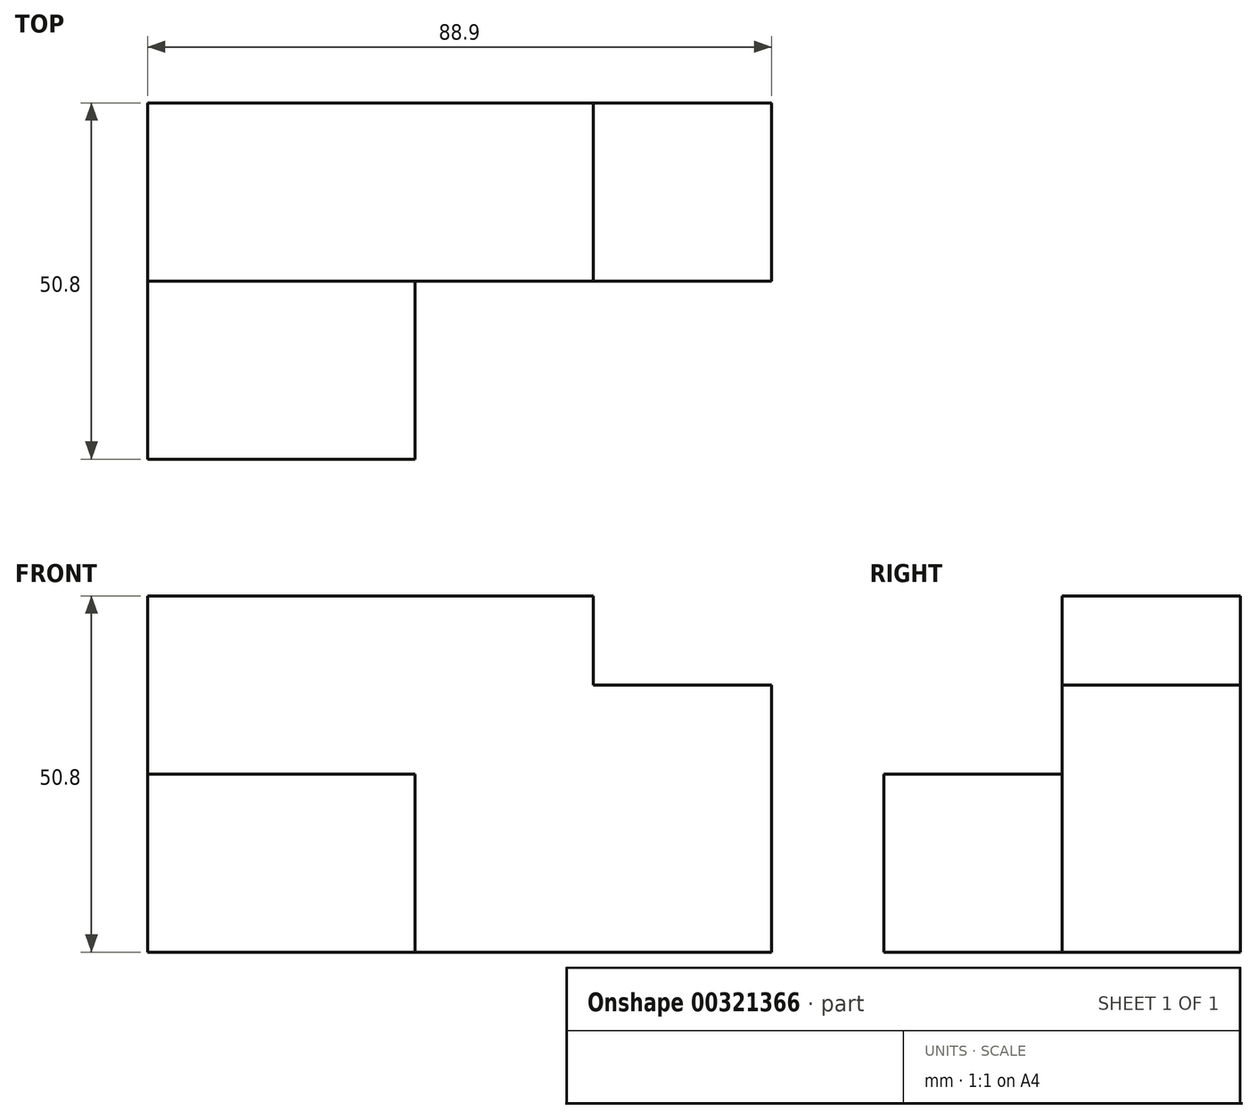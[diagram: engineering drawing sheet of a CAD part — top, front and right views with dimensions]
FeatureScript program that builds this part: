
annotation { "Feature Type Name" : "Feature", "Feature Type Description" : "" }
export const myFeature = defineFeature(function(context is Context, id is Id, definition is map)
    precondition{}
    {
        {
            var Q0;
            Q0=qCreatedBy(makeId("Front.planeOp"),FACE);
            var sketch = newSketch(context, id + "F0", { "sketchPlane" : qUnion([Q0])});
            skLineSegment(sketch, "E0", {"start": v(-32.5, 6.18) * mm, "end": v(31, 6.18) * mm});
            skLineSegment(sketch, "E1", {"start": v(31, 6.18) * mm, "end": v(31, -6.52) * mm});
            skLineSegment(sketch, "E2", {"start": v(31, -6.52) * mm, "end": v(56.4, -6.52) * mm});
            skLineSegment(sketch, "E3", {"start": v(56.4, -6.52) * mm, "end": v(56.4, -44.62) * mm});
            skLineSegment(sketch, "E4", {"start": v(56.4, -44.62) * mm, "end": v(-32.5, -44.62) * mm});
            skLineSegment(sketch, "E5", {"start": v(-32.5, -44.62) * mm, "end": v(-32.5, 6.18) * mm});
            skSolve(sketch);
        }
        {
            var Q0;
            Q0=makeQuery(id+"F0.imprint","IMPRINT",FACE,{"disambiguationData":[TD([[makeQuery(id+"F0.imprint","IMPRINT",EDGE,{"derivedFrom":sQuery(id+"F0.wireOp",EDGE,"E0")}),-1.0]])]});
            extrude(context, id + "F1", {"entities" : qUnion([Q0]), "oppositeDirection" : true, "depth" : 25.4 * mm});
        }
        {
            var Q0;
            Q0=makeQuery(id+"F1.opExtrude","CAP_FACE",FACE,{"disambiguationData":[OSD([sQuery(id+"F0.wireOp",EDGE,"E0"),sQuery(id+"F0.wireOp",EDGE,"E1"),sQuery(id+"F0.wireOp",EDGE,"E2"),sQuery(id+"F0.wireOp",EDGE,"E3"),sQuery(id+"F0.wireOp",EDGE,"E4"),sQuery(id+"F0.wireOp",EDGE,"E5")])],"isStart":true});
            var sketch = newSketch(context, id + "F2", { "sketchPlane" : qUnion([Q0])});
            skLineSegment(sketch, "E6", {"start": v(-32.5, -44.62) * mm, "end": v(-32.5, -19.22) * mm});
            skLineSegment(sketch, "E7", {"start": v(-32.5, -19.22) * mm, "end": v(5.6, -19.22) * mm});
            skLineSegment(sketch, "E8", {"start": v(5.6, -19.22) * mm, "end": v(5.6, -44.62) * mm});
            skLineSegment(sketch, "E9", {"start": v(5.6, -44.62) * mm, "end": v(-32.5, -44.62) * mm});
            skSolve(sketch);
        }
        {
            var Q0;
            Q0=makeQuery(id+"F2.imprint","IMPRINT",FACE,{"disambiguationData":[TD([[makeQuery(id+"F2.imprint","IMPRINT",EDGE,{"derivedFrom":sQuery(id+"F2.wireOp",EDGE,"E6")}),-1.0]])]});
            extrude(context, id + "F3", {"entities" : qUnion([Q0]), "operationType" : NewBodyOperationType.ADD, "depth" : 25.4 * mm});
        }
    });
